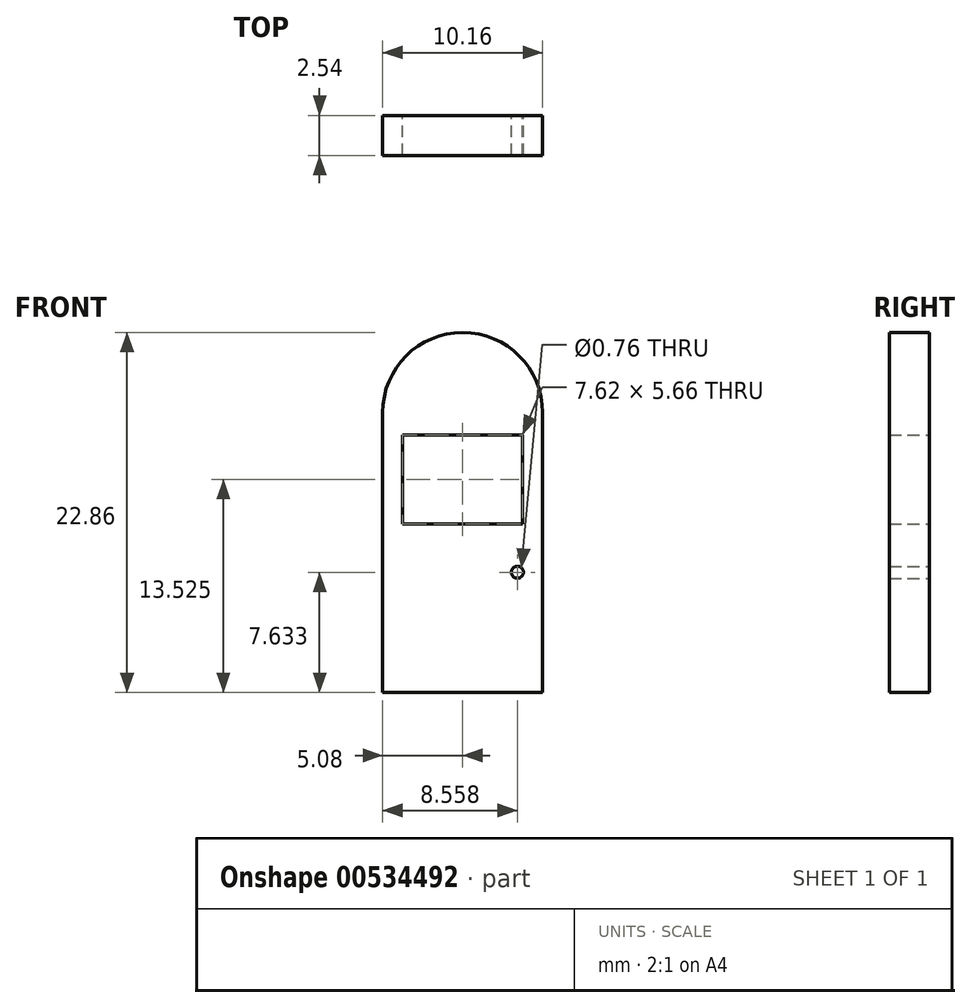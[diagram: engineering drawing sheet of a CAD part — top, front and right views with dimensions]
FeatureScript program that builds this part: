
annotation { "Feature Type Name" : "Feature", "Feature Type Description" : "" }
export const myFeature = defineFeature(function(context is Context, id is Id, definition is map)
    precondition{}
    {
        {
            var Q0;
            Q0=qCreatedBy(makeId("Front.planeOp"),FACE);
            var sketch = newSketch(context, id + "F0", { "sketchPlane" : qUnion([Q0])});
            skLineSegment(sketch, "E0.bottom", {"start": v(0, 0) * mm, "end": v(-10.16, 0) * mm});
            skLineSegment(sketch, "E0.top", {"start": v(0, 17.78) * mm, "end": v(-10.16, 17.78) * mm});
            skLineSegment(sketch, "E0.left", {"start": v(0, 0) * mm, "end": v(0, 17.78) * mm});
            skLineSegment(sketch, "E0.right", {"start": v(-10.16, 0) * mm, "end": v(-10.16, 17.78) * mm});
            skArc(sketch, "E1", {"start": v(0, 17.78) * mm, "mid": v(-5.08, 22.86) * mm, "end": v(-10.16, 17.78) * mm});
            skCircle(sketch, "E2", {"center": v(-1.6, 7.63) * mm, "radius": 0.38 * mm});
            skLineSegment(sketch, "E3.bottom", {"start": v(-8.9, 16.36) * mm, "end": v(-1.27, 16.36) * mm});
            skLineSegment(sketch, "E3.top", {"start": v(-8.9, 10.7) * mm, "end": v(-1.27, 10.7) * mm});
            skLineSegment(sketch, "E3.left", {"start": v(-8.9, 16.36) * mm, "end": v(-8.9, 10.7) * mm});
            skLineSegment(sketch, "E3.right", {"start": v(-1.27, 16.36) * mm, "end": v(-1.27, 10.7) * mm});
            skLineSegment(sketch, "E4", {"start": v(-8.9, 13.52) * mm, "end": v(-1.27, 13.52) * mm});
            skLineSegment(sketch, "E5", {"start": v(-5.08, 16.36) * mm, "end": v(-5.08, 10.7) * mm});
            skSolve(sketch);
        }
        {
            var Q0;
            Q0=makeQuery(id+"F0.imprint","IMPRINT",FACE,{"disambiguationData":[TD([[makeQuery(id+"F0.imprint","IMPRINT",EDGE,{"derivedFrom":sQuery(id+"F0.wireOp",EDGE,"E0.bottom")}),-1.0]])]});
            var Q1;
            Q1=makeQuery(id+"F0.imprint","IMPRINT",FACE,{"disambiguationData":[TD([[makeQuery(id+"F0.imprint","IMPRINT",EDGE,{"derivedFrom":sQuery(id+"F0.wireOp",EDGE,"E0.top")}),-1.0]])]});
            extrude(context, id + "F1", {"entities" : qUnion([Q0, Q1]), "endBound" : BoundingType.SYMMETRIC, "depth" : 2.54 * mm, "offsetDistance" : 25.4 * mm});
        }
    });
